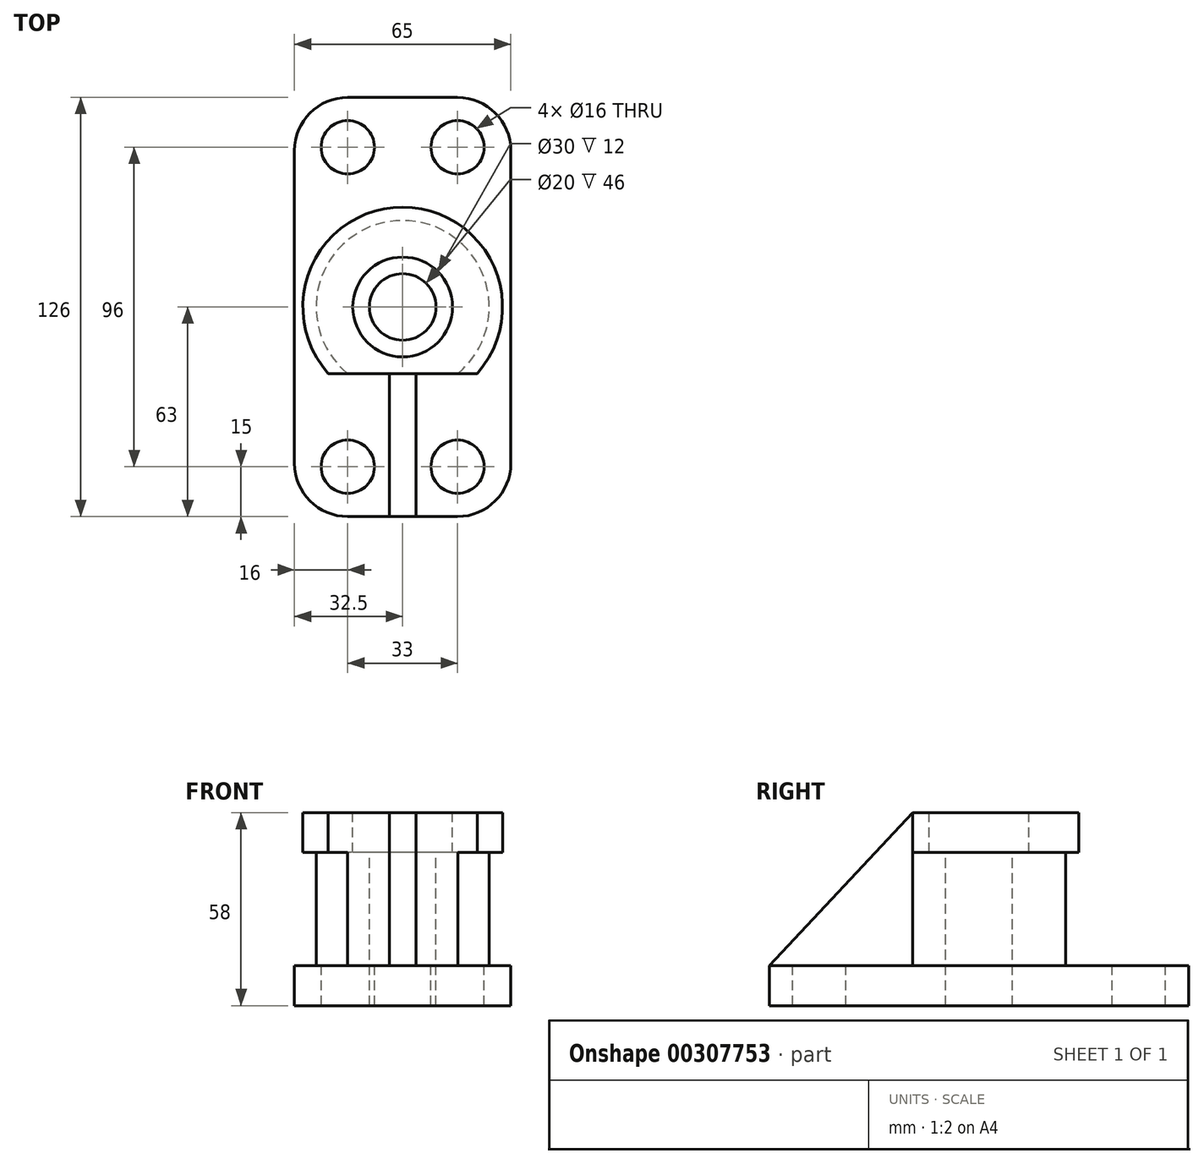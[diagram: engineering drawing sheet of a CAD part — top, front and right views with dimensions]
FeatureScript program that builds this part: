
annotation { "Feature Type Name" : "Feature", "Feature Type Description" : "" }
export const myFeature = defineFeature(function(context is Context, id is Id, definition is map)
    precondition{}
    {
        {
            var Q0;
            Q0=qCreatedBy(makeId("Top.planeOp"),FACE);
            var sketch = newSketch(context, id + "F0", { "sketchPlane" : qUnion([Q0])});
            skLineSegment(sketch, "E0.bottom", {"start": v(32.5, 63) * mm, "end": v(-32.5, 63) * mm});
            skLineSegment(sketch, "E0.top", {"start": v(32.5, -63) * mm, "end": v(-32.5, -63) * mm});
            skLineSegment(sketch, "E0.left", {"start": v(32.5, 63) * mm, "end": v(32.5, -63) * mm});
            skLineSegment(sketch, "E0.right", {"start": v(-32.5, 63) * mm, "end": v(-32.5, -63) * mm});
            skPoint(sketch, "E0.middle", {"position": v(0, 0) * mm});
            skSolve(sketch);
        }
        {
            var Q0;
            Q0 = qSketchRegion(id + "F0", true);
            extrude(context, id + "F1", {"entities" : qUnion([Q0]), "depth" : 12 * mm});
        }
        {
            var Q0;
            Q0=makeQuery(id+"F1.opExtrude","SWEPT_EDGE",EDGE,{"disambiguationData":[OSD([sQuery(id+"F0.wireOp",EDGE,"E0.top"),sQuery(id+"F0.wireOp",EDGE,"E0.left")])]});
            var Q1;
            Q1=makeQuery(id+"F1.opExtrude","SWEPT_EDGE",EDGE,{"disambiguationData":[OSD([sQuery(id+"F0.wireOp",EDGE,"E0.top"),sQuery(id+"F0.wireOp",EDGE,"E0.right")])]});
            var Q2;
            Q2=makeQuery(id+"F1.opExtrude","SWEPT_EDGE",EDGE,{"disambiguationData":[OSD([sQuery(id+"F0.wireOp",EDGE,"E0.bottom"),sQuery(id+"F0.wireOp",EDGE,"E0.left")])]});
            var Q3;
            Q3=makeQuery(id+"F1.opExtrude","SWEPT_EDGE",EDGE,{"disambiguationData":[OSD([sQuery(id+"F0.wireOp",EDGE,"E0.bottom"),sQuery(id+"F0.wireOp",EDGE,"E0.right")])]});
            fillet(context, id + "F2", {"entities" : qUnion([Q0, Q1, Q2, Q3]), "radius" : 16 * mm, "tangentPropagation" : true, "allowEdgeOverflow" : false});
        }
        {
            var Q0;
            Q0=makeQuery(id+"F1.opExtrude","CAP_FACE",FACE,{"disambiguationData":[OSD([sQuery(id+"F0.wireOp",EDGE,"E0.bottom"),sQuery(id+"F0.wireOp",EDGE,"E0.top"),sQuery(id+"F0.wireOp",EDGE,"E0.left"),sQuery(id+"F0.wireOp",EDGE,"E0.right")])],"isStart":false});
            var sketch = newSketch(context, id + "F3", { "sketchPlane" : qUnion([Q0])});
            skCircle(sketch, "E1", {"center": v(-16.5, 48) * mm, "radius": 8 * mm});
            skCircle(sketch, "E2", {"center": v(16.5, 48) * mm, "radius": 8 * mm});
            skCircle(sketch, "E3", {"center": v(16.5, -48) * mm, "radius": 8 * mm});
            skCircle(sketch, "E4", {"center": v(-16.5, -48) * mm, "radius": 8 * mm});
            skSolve(sketch);
        }
        {
            var Q0;
            Q0 = qSketchRegion(id + "F3", true);
            var Q1;
            Q1=makeQuery(id+"F1.opExtrude","CAP_FACE",FACE,{"disambiguationData":[OSD([sQuery(id+"F0.wireOp",EDGE,"E0.bottom"),sQuery(id+"F0.wireOp",EDGE,"E0.top"),sQuery(id+"F0.wireOp",EDGE,"E0.left"),sQuery(id+"F0.wireOp",EDGE,"E0.right")])],"isStart":true});
            extrude(context, id + "F4", {"entities" : qUnion([Q0]), "operationType" : NewBodyOperationType.REMOVE, "endBound" : BoundingType.UP_TO_SURFACE, "oppositeDirection" : true, "endBoundEntityFace" : qUnion([Q1]), "depth" : 25 * mm});
        }
        {
            var Q0;
            Q0=makeQuery(id+"F1.opExtrude","CAP_FACE",FACE,{"disambiguationData":[OSD([sQuery(id+"F0.wireOp",EDGE,"E0.bottom"),sQuery(id+"F0.wireOp",EDGE,"E0.top"),sQuery(id+"F0.wireOp",EDGE,"E0.left"),sQuery(id+"F0.wireOp",EDGE,"E0.right")])],"isStart":false});
            var sketch = newSketch(context, id + "F5", { "sketchPlane" : qUnion([Q0])});
            skCircle(sketch, "E5", {"center": v(0, 0) * mm, "radius": 26 * mm});
            skSolve(sketch);
        }
        {
            var Q0;
            Q0 = qSketchRegion(id + "F5", true);
            extrude(context, id + "F6", {"entities" : qUnion([Q0]), "operationType" : NewBodyOperationType.ADD, "depth" : 34 * mm});
        }
        {
            var Q0;
            Q0=makeQuery(id+"F6.opExtrude","CAP_FACE",FACE,{"disambiguationData":[OSD([sQuery(id+"F5.wireOp",EDGE,"E5")])],"isStart":false});
            var sketch = newSketch(context, id + "F7", { "sketchPlane" : qUnion([Q0])});
            skCircle(sketch, "E6", {"center": v(0, 0) * mm, "radius": 30 * mm});
            skSolve(sketch);
        }
        {
            var Q0;
            Q0 = qSketchRegion(id + "F7", true);
            extrude(context, id + "F8", {"entities" : qUnion([Q0]), "operationType" : NewBodyOperationType.ADD, "depth" : 12 * mm});
        }
        {
            var Q0;
            Q0=makeQuery(id+"F8.opExtrude","CAP_FACE",FACE,{"disambiguationData":[OSD([sQuery(id+"F7.wireOp",EDGE,"E6")])],"isStart":false});
            var sketch = newSketch(context, id + "F9", { "sketchPlane" : qUnion([Q0])});
            skCircle(sketch, "E7", {"center": v(0, 0) * mm, "radius": 15 * mm});
            skSolve(sketch);
        }
        {
            var Q0;
            Q0 = qSketchRegion(id + "F9", true);
            extrude(context, id + "F10", {"entities" : qUnion([Q0]), "operationType" : NewBodyOperationType.REMOVE, "oppositeDirection" : true, "depth" : 12 * mm});
        }
        {
            var Q0;
            Q0=makeQuery(id+"F10.boolean.opBoolean","COPY",FACE,{"derivedFrom":makeQuery(id+"F10.opExtrude","CAP_FACE",FACE,{"disambiguationData":[OSD([sQuery(id+"F9.wireOp",EDGE,"E7")])],"isStart":false})});
            var sketch = newSketch(context, id + "F11", { "sketchPlane" : qUnion([Q0])});
            skCircle(sketch, "E8", {"center": v(0, 0) * mm, "radius": 10 * mm});
            skSolve(sketch);
        }
        {
            var Q0;
            Q0 = qSketchRegion(id + "F11", true);
            var Q1;
            Q1=makeQuery(id+"F1.opExtrude","CAP_FACE",FACE,{"disambiguationData":[OSD([sQuery(id+"F0.wireOp",EDGE,"E0.bottom"),sQuery(id+"F0.wireOp",EDGE,"E0.top"),sQuery(id+"F0.wireOp",EDGE,"E0.left"),sQuery(id+"F0.wireOp",EDGE,"E0.right")])],"isStart":true});
            extrude(context, id + "F12", {"entities" : qUnion([Q0]), "operationType" : NewBodyOperationType.REMOVE, "endBound" : BoundingType.UP_TO_SURFACE, "oppositeDirection" : true, "endBoundEntityFace" : qUnion([Q1]), "depth" : 25 * mm});
        }
        {
            var Q0;
            Q0=makeQuery(id+"F8.opExtrude","CAP_FACE",FACE,{"disambiguationData":[OSD([sQuery(id+"F7.wireOp",EDGE,"E6")])],"isStart":false});
            var sketch = newSketch(context, id + "F13", { "sketchPlane" : qUnion([Q0])});
            skLineSegment(sketch, "E9", {"start": v(-22.36, -20) * mm, "end": v(22.36, -20) * mm});
            skArc(sketch, "E10", {"start": v(-22.36, -20) * mm, "mid": v(0, -30) * mm, "end": v(22.36, -20) * mm});
            skSolve(sketch);
        }
        {
            var Q0;
            Q0 = qSketchRegion(id + "F13", true);
            var Q1;
            Q1=makeQuery(id+"F1.opExtrude","CAP_FACE",FACE,{"disambiguationData":[OSD([sQuery(id+"F0.wireOp",EDGE,"E0.bottom"),sQuery(id+"F0.wireOp",EDGE,"E0.top"),sQuery(id+"F0.wireOp",EDGE,"E0.left"),sQuery(id+"F0.wireOp",EDGE,"E0.right")])],"isStart":false});
            extrude(context, id + "F14", {"entities" : qUnion([Q0]), "operationType" : NewBodyOperationType.REMOVE, "endBound" : BoundingType.UP_TO_SURFACE, "oppositeDirection" : true, "endBoundEntityFace" : qUnion([Q1]), "depth" : 25 * mm});
        }
        {
            var Q0;
            {var subQ0=sQuery(id+"F0.wireOp",EDGE,"E0.right");var subQ1=sQuery(id+"F0.wireOp",EDGE,"E0.left");var subQ2=sQuery(id+"F0.wireOp",EDGE,"E0.top");var subQ3=sQuery(id+"F0.wireOp",EDGE,"E0.bottom");Q0=makeQuery(id+"F14.boolean.opBoolean","MERGE",FACE,{"derivedFrom":[makeQuery(id+"F1.opExtrude","CAP_FACE",FACE,{"disambiguationData":[OSD([subQ3,subQ2,subQ1,subQ0])],"isStart":false}),makeQuery(id+"F14.opExtrude","CAP_FACE",FACE,{"disambiguationData":[OSD([subQ3,subQ2,subQ1,subQ0])],"isStart":false})]});}
            var sketch = newSketch(context, id + "F15", { "sketchPlane" : qUnion([Q0])});
            skLineSegment(sketch, "E11", {"start": v(-4, -63) * mm, "end": v(-4, -20) * mm});
            skLineSegment(sketch, "E12", {"start": v(-4, -20) * mm, "end": v(4, -20) * mm});
            skLineSegment(sketch, "E13", {"start": v(4, -20) * mm, "end": v(4, -63) * mm});
            skLineSegment(sketch, "E14", {"start": v(4, -63) * mm, "end": v(-4, -63) * mm});
            skSolve(sketch);
        }
        {
            var Q0;
            Q0 = qSketchRegion(id + "F15", true);
            var Q1;
            Q1=makeQuery(id+"F8.opExtrude","CAP_FACE",FACE,{"disambiguationData":[OSD([sQuery(id+"F7.wireOp",EDGE,"E6")])],"isStart":false});
            extrude(context, id + "F16", {"entities" : qUnion([Q0]), "operationType" : NewBodyOperationType.ADD, "endBound" : BoundingType.UP_TO_SURFACE, "endBoundEntityFace" : qUnion([Q1]), "depth" : 25 * mm});
        }
        {
            var Q0;
            Q0=makeQuery(id+"F16.opExtrude","SWEPT_FACE",FACE,{"disambiguationData":[OSD([sQuery(id+"F15.wireOp",EDGE,"E13")])]});
            var sketch = newSketch(context, id + "F17", { "sketchPlane" : qUnion([Q0])});
            skLineSegment(sketch, "E15", {"start": v(-20, 58) * mm, "end": v(-63, 12) * mm});
            skLineSegment(sketch, "E16", {"start": v(-63, 12) * mm, "end": v(-63, 58) * mm});
            skLineSegment(sketch, "E17", {"start": v(-63, 58) * mm, "end": v(-20, 58) * mm});
            skSolve(sketch);
        }
        {
            var Q0;
            Q0 = qSketchRegion(id + "F17", true);
            var Q1;
            Q1=makeQuery(id+"F16.opExtrude","SWEPT_FACE",FACE,{"disambiguationData":[OSD([sQuery(id+"F15.wireOp",EDGE,"E11")])]});
            extrude(context, id + "F18", {"entities" : qUnion([Q0]), "operationType" : NewBodyOperationType.REMOVE, "endBound" : BoundingType.UP_TO_SURFACE, "oppositeDirection" : true, "endBoundEntityFace" : qUnion([Q1]), "depth" : 25 * mm});
        }
    });
